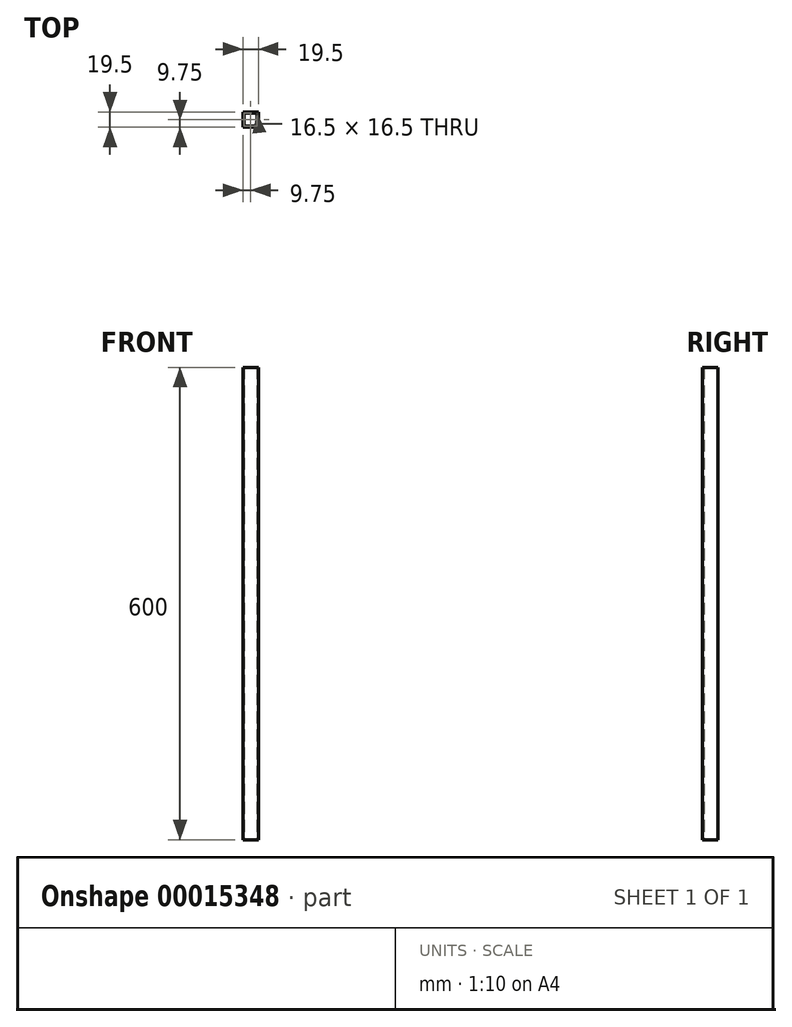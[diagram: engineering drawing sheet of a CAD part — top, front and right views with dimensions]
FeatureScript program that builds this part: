
annotation { "Feature Type Name" : "Feature", "Feature Type Description" : "" }
export const myFeature = defineFeature(function(context is Context, id is Id, definition is map)
    precondition{}
    {
        {
            var Q0;
            Q0=qCreatedBy(makeId("Top.planeOp"),FACE);
            var sketch = newSketch(context, id + "F0", { "sketchPlane" : qUnion([Q0])});
            skLineSegment(sketch, "E0.bottom", {"start": v(0, 0) * mm, "end": v(19.5, 0) * mm});
            skLineSegment(sketch, "E0.top", {"start": v(0, 19.5) * mm, "end": v(19.5, 19.5) * mm});
            skLineSegment(sketch, "E0.left", {"start": v(0, 0) * mm, "end": v(0, 19.5) * mm});
            skLineSegment(sketch, "E0.right", {"start": v(19.5, 0) * mm, "end": v(19.5, 19.5) * mm});
            skLineSegment(sketch, "E1.0", {"start": v(18, 1.5) * mm, "end": v(18, 18) * mm});
            skLineSegment(sketch, "E1.1", {"start": v(1.5, 1.5) * mm, "end": v(18, 1.5) * mm});
            skLineSegment(sketch, "E1.2", {"start": v(1.5, 1.5) * mm, "end": v(1.5, 18) * mm});
            skLineSegment(sketch, "E1.3", {"start": v(1.5, 18) * mm, "end": v(18, 18) * mm});
            skLineSegment(sketch, "E2", {"start": v(9.75, 19.5) * mm, "end": v(9.75, 0) * mm});
            skSolve(sketch);
        }
        {
            var Q0;
            Q0=makeQuery(id+"F0.imprint","IMPRINT",FACE,{"disambiguationData":[TD([[makeQuery(id+"F0.imprint","IMPRINT",EDGE,{"derivedFrom":sQuery(id+"F0.wireOp",EDGE,"E0.bottom")}),1.0]])]});
            extrude(context, id + "F1", {"entities" : qUnion([Q0]), "depth" : 600 * mm});
        }
    });
